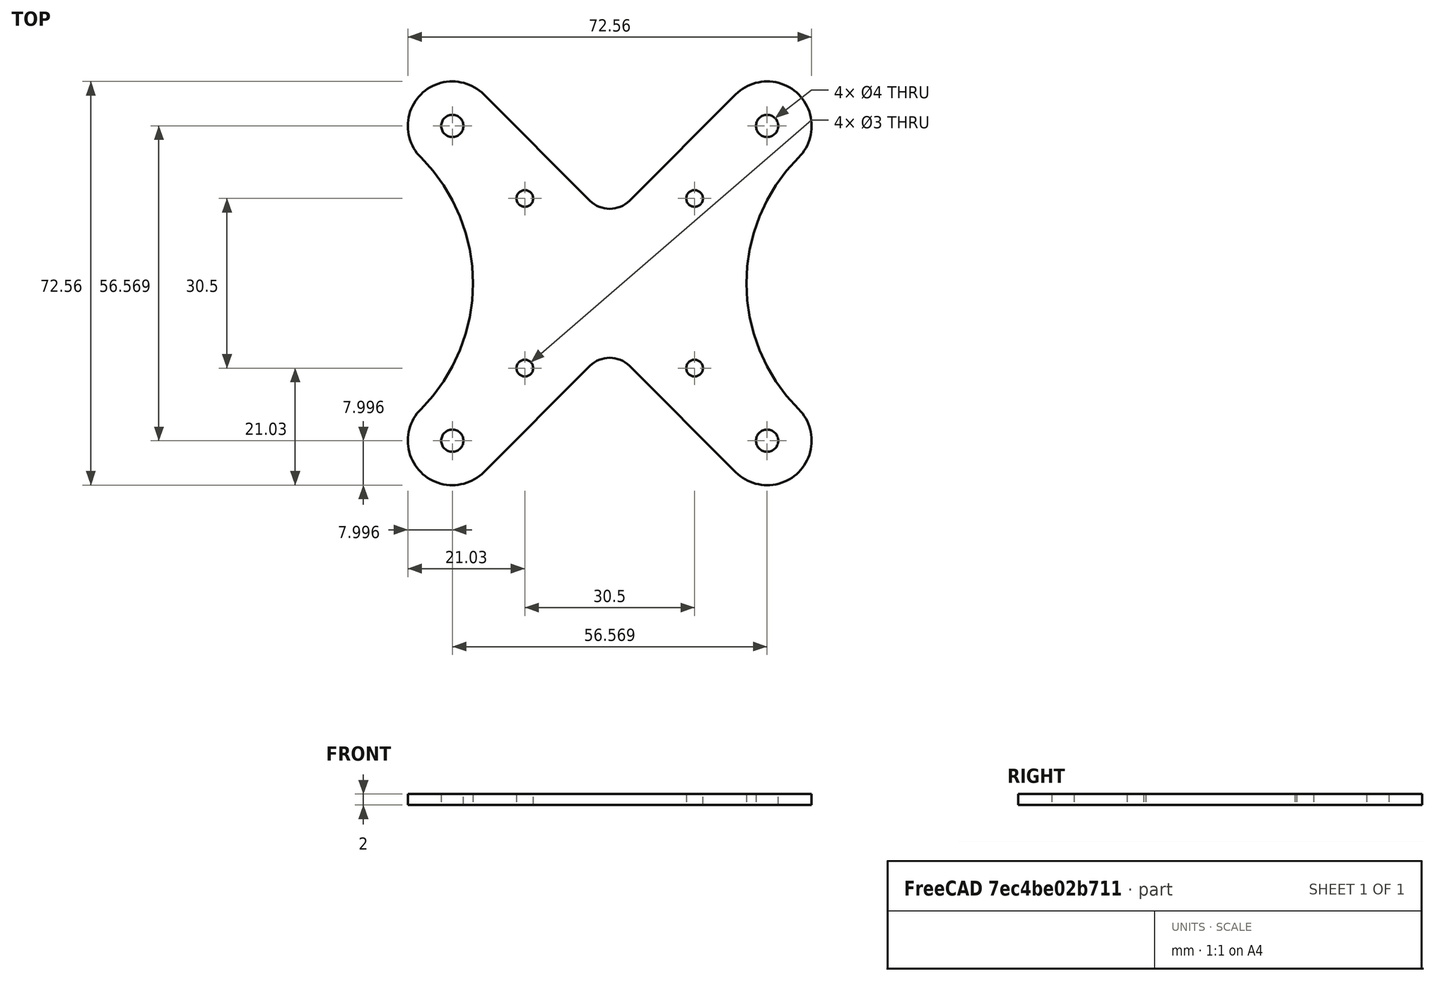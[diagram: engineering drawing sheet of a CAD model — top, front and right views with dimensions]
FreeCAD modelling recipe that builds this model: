
FCSTD DOCUMENT  (FreeCAD 0.18RUnknown)
Label: bottom
License: All rights reserved
LicenseURL: http://en.wikipedia.org/wiki/All_rights_reserved
objects: Sketcher::SketchObject×1, Part::Extrusion×1
note: 2 computed .brp shape members not serialized (recipe doc carries the construction recipe); baked Part::Feature solids carry a one-line shape summary decoded from their .brp

FEATURE [Sketcher::SketchObject] Sketch
  expr: Constraints[43] = anomaly#Spreadsheet.armHoleCenterOffset
  expr: Constraints[4] = anomaly#Spreadsheet.electroMounting
  sketch-geometry (29):
    g0: LineSegment [constr] StartX=-15.25 StartY=15.25 StartZ=0 EndX=15.25 EndY=15.25 EndZ=0
    g1: LineSegment [constr] StartX=15.25 StartY=-15.25 StartZ=0 EndX=-15.25 EndY=-15.25 EndZ=0
    g2: LineSegment [constr] StartX=-15.25 StartY=-15.25 StartZ=0 EndX=-15.25 EndY=15.25 EndZ=0
    g3: Circle CenterX=28.2843 CenterY=28.2843 CenterZ=0 NormalX=0 NormalY=0 NormalZ=1 AngleXU=0 Radius=2
    g4: Circle CenterX=28.2843 CenterY=-28.2843 CenterZ=0 NormalX=0 NormalY=0 NormalZ=1 AngleXU=0 Radius=2
    g5: Circle CenterX=-28.2843 CenterY=-28.2843 CenterZ=0 NormalX=0 NormalY=0 NormalZ=1 AngleXU=0 Radius=2
    g6: Circle CenterX=-28.2843 CenterY=28.2843 CenterZ=0 NormalX=0 NormalY=0 NormalZ=1 AngleXU=0 Radius=2
    g7: ArcOfCircle CenterX=-28.2843 CenterY=28.2843 CenterZ=0 NormalX=0 NormalY=0 NormalZ=1 AngleXU=0 Radius=8 StartAngle=0.785398 EndAngle=3.92699
    g8: ArcOfCircle CenterX=-28.2843 CenterY=-28.2843 CenterZ=0 NormalX=0 NormalY=0 NormalZ=1 AngleXU=0 Radius=8 StartAngle=2.35619 EndAngle=5.49779
    g9: ArcOfCircle CenterX=28.2843 CenterY=-28.2843 CenterZ=0 NormalX=0 NormalY=0 NormalZ=1 AngleXU=0 Radius=8 StartAngle=3.92699 EndAngle=7.06858
    g10: ArcOfCircle CenterX=28.2843 CenterY=28.2843 CenterZ=0 NormalX=0 NormalY=0 NormalZ=1 AngleXU=0 Radius=8 StartAngle=5.49779 EndAngle=8.63938
    g11: GeomPoint X=22.6274 Y=33.9411 Z=0
    g12: LineSegment [constr] StartX=15.25 StartY=15.25 StartZ=0 EndX=15.25 EndY=-15.25 EndZ=0
    g13: LineSegment [constr] StartX=-28.2843 StartY=28.2843 StartZ=0 EndX=28.2843 EndY=28.2843 EndZ=0
    g14: LineSegment [constr] StartX=28.2843 StartY=28.2843 StartZ=0 EndX=28.2843 EndY=-28.2843 EndZ=0
    g15: LineSegment [constr] StartX=28.2843 StartY=-28.2843 StartZ=0 EndX=-28.2843 EndY=-28.2843 EndZ=0
    g16: LineSegment [constr] StartX=-28.2843 StartY=-28.2843 StartZ=0 EndX=-28.2843 EndY=28.2843 EndZ=0
    g17: ArcOfCircle CenterX=56.5685 CenterY=0 CenterZ=0 NormalX=0 NormalY=0 NormalZ=1 AngleXU=0 Radius=32 StartAngle=2.35619 EndAngle=3.92699
    g18: ArcOfCircle CenterX=-56.5685 CenterY=0 CenterZ=0 NormalX=0 NormalY=0 NormalZ=1 AngleXU=0 Radius=32 StartAngle=5.49779 EndAngle=7.06858
    g19: LineSegment StartX=-22.6274 StartY=33.9411 StartZ=0 EndX=-3.53553 EndY=14.8492 EndZ=0
    g20: LineSegment StartX=3.53553 StartY=14.8492 StartZ=0 EndX=22.6274 EndY=33.9411 EndZ=0
    g21: LineSegment StartX=3.53553 StartY=-14.8492 StartZ=0 EndX=22.6274 EndY=-33.9411 EndZ=0
    g22: LineSegment StartX=-22.6274 StartY=-33.9411 StartZ=0 EndX=-3.53553 EndY=-14.8492 EndZ=0
    g23: ArcOfCircle CenterX=0 CenterY=18.3848 CenterZ=0 NormalX=0 NormalY=0 NormalZ=1 AngleXU=0 Radius=5 StartAngle=3.92699 EndAngle=5.49779
    g24: ArcOfCircle CenterX=0 CenterY=-18.3848 CenterZ=0 NormalX=0 NormalY=0 NormalZ=1 AngleXU=0 Radius=5 StartAngle=0.785398 EndAngle=2.35619
    g25: Circle CenterX=15.25 CenterY=15.25 CenterZ=0 NormalX=0 NormalY=0 NormalZ=1 AngleXU=0 Radius=1.5
    g26: Circle CenterX=-15.25 CenterY=15.25 CenterZ=0 NormalX=0 NormalY=0 NormalZ=1 AngleXU=0 Radius=1.5
    g27: Circle CenterX=-15.25 CenterY=-15.25 CenterZ=0 NormalX=0 NormalY=0 NormalZ=1 AngleXU=0 Radius=1.5
    g28: Circle CenterX=15.25 CenterY=-15.25 CenterZ=0 NormalX=0 NormalY=0 NormalZ=1 AngleXU=0 Radius=1.5
  constraints (66):
    c: Coincident(g1,g2)
    c: Horizontal(g0)
    c: Horizontal(g1)
    c: Vertical(g2)
    c: DistanceY(g1,g0) = 30.5
    c: Equal(g7,g8)
    c: Equal(g8,g9)
    c: Equal(g9,g10)
    c: Coincident(g12,g0)
    c: Coincident(g12,g1)
    c: Vertical(g12)
    c: Coincident(g0,g2)
    c: Coincident(g13,g14)
    c: Coincident(g14,g15)
    c: Coincident(g15,g16)
    c: Coincident(g16,g13)
    c: Horizontal(g13)
    c: Horizontal(g15)
    c: Vertical(g14)
    c: Vertical(g16)
    c: Coincident(g13,g3)
    c: Coincident(g10,g3)
    c: Coincident(g14,g4)
    c: Coincident(g9,g4)
    c: Coincident(g15,g5)
    c: Coincident(g5,g8)
    c: Coincident(g13,g6)
    c: Coincident(g6,g7)
    c: Symmetric(g0,g1,g-1)
    c: Symmetric(g6,g4,g-1)
    c: Equal(g13,g16)
    c: Equal(g2,g0)
    c: Coincident(g10,g11) = 1.5708
    c: Radius(g10) = 8
    c: Tangent(g18,g7) = 1.5708
    c: Tangent(g18,g8) = 1.5708
    c: Tangent(g17,g10) = 1.5708
    c: Tangent(g17,g9) = 1.5708
    c: Equal(g17,g18)
    c: Tangent(g19,g23) = -1.5708
    c: Tangent(g20,g23) = -1.5708
    c: Tangent(g22,g24) = 1.5708
    c: Tangent(g21,g24) = 1.5708
    c: Distance(g-1,g3) = 40
    c: Equal(g3,g6)
    c: Equal(g6,g5)
    c: Equal(g5,g4)
    c: Radius(g3) = 2
    c: Radius(g18) = 32
    c: Tangent(g19,g7) = 1.5708
    c: Tangent(g20,g10) = 1.5708
    c: Tangent(g8,g22) = -1.5708
    c: Tangent(g21,g9) = -1.5708
    c: PointOnObject(g23,g-2)
    c: Angle(g20,g19) = 1.5708
    c: Symmetric(g24,g23,g-1)
    c: Radius(g24) = 5
    c: Equal(g24,g23)
    c: Coincident(g25,g0)
    c: Coincident(g26,g0)
    c: Coincident(g27,g1)
    c: Coincident(g28,g1)
    c: Equal(g28,g25)
    c: Equal(g25,g26)
    c: Equal(g26,g27)
    c: Radius(g25) = 1.5
FEATURE [Part::Extrusion] Extrude
  Base = -> Sketch
  Dir = (0,0,1)
  DirMode = 2
  FaceMakerClass = Part::FaceMakerBullseye
  LengthFwd = 2
  LengthRev = 0
  Solid = true
  Symmetric = false
